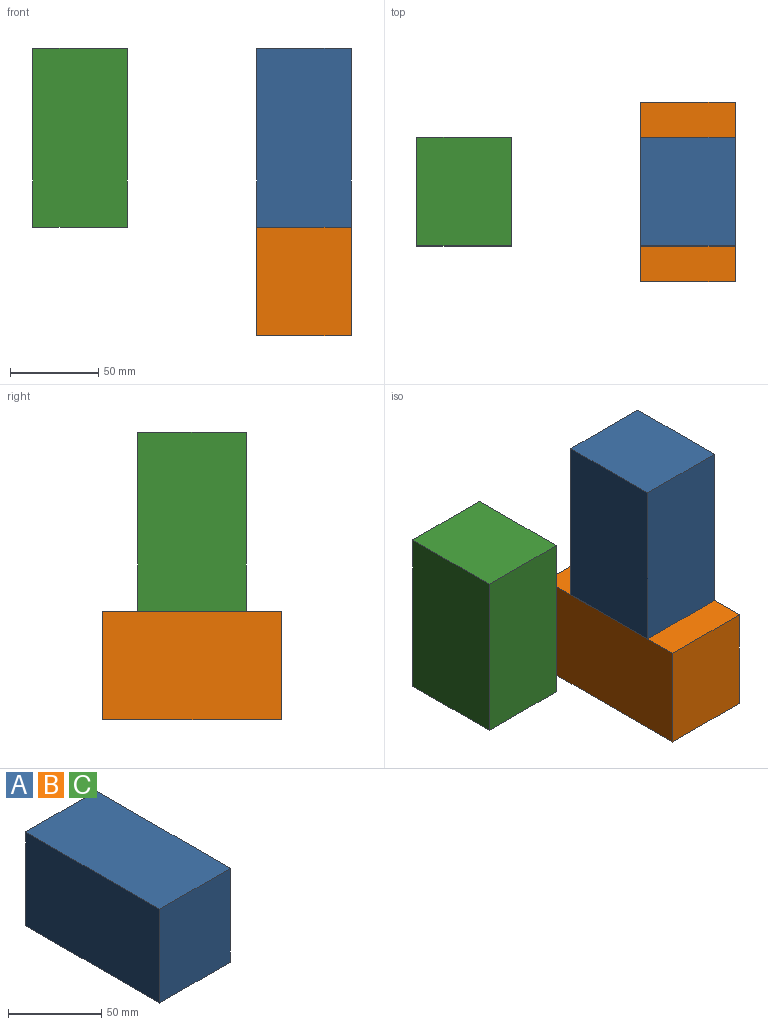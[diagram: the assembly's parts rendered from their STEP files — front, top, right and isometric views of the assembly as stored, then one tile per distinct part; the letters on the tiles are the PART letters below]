
ASSEMBLY  parts=3 mates=1
PART A: 6 faces, bbox 53.7x101.6x61.6 mm
  f0: plane 101.6x53.74mm, normal (0,0,1), area 5460.4mm2, adj f1,f3,f4,f5
  f1: plane 101.6x61.57mm, normal (-1,0,0), area 6255.6mm2, adj f0,f2,f4,f5
  f2: plane 101.6x53.74mm, normal (0,0,-1), area 5460.4mm2, adj f1,f3,f4,f5
  f3: plane 101.6x61.57mm, normal (1,0,0), area 6255.6mm2, adj f0,f2,f4,f5
  f4: plane 61.57x53.74mm, normal (0,1,0), area 3309.1mm2, adj f0,f1,f2,f3
  f5: plane 61.57x53.74mm, normal (0,-1,0), area 3309.1mm2, adj f0,f1,f2,f3
PART B: same geometry as A
PART C: same geometry as A
PLACE A rot(axis=(0,0.71,0.71),180deg) t=(-64.16,-30.07,64.16)mm
PLACE B t=(-10.42,-50.08,2.59)mm fixed
PLACE C rot(axis=(0,0.71,0.71),180deg) t=(-191.16,-30.07,64.16)mm
MATE fastened A.f5 <-> B.f0  axis (0,0,-1) through (-37.29,0.72,64.16)mm
